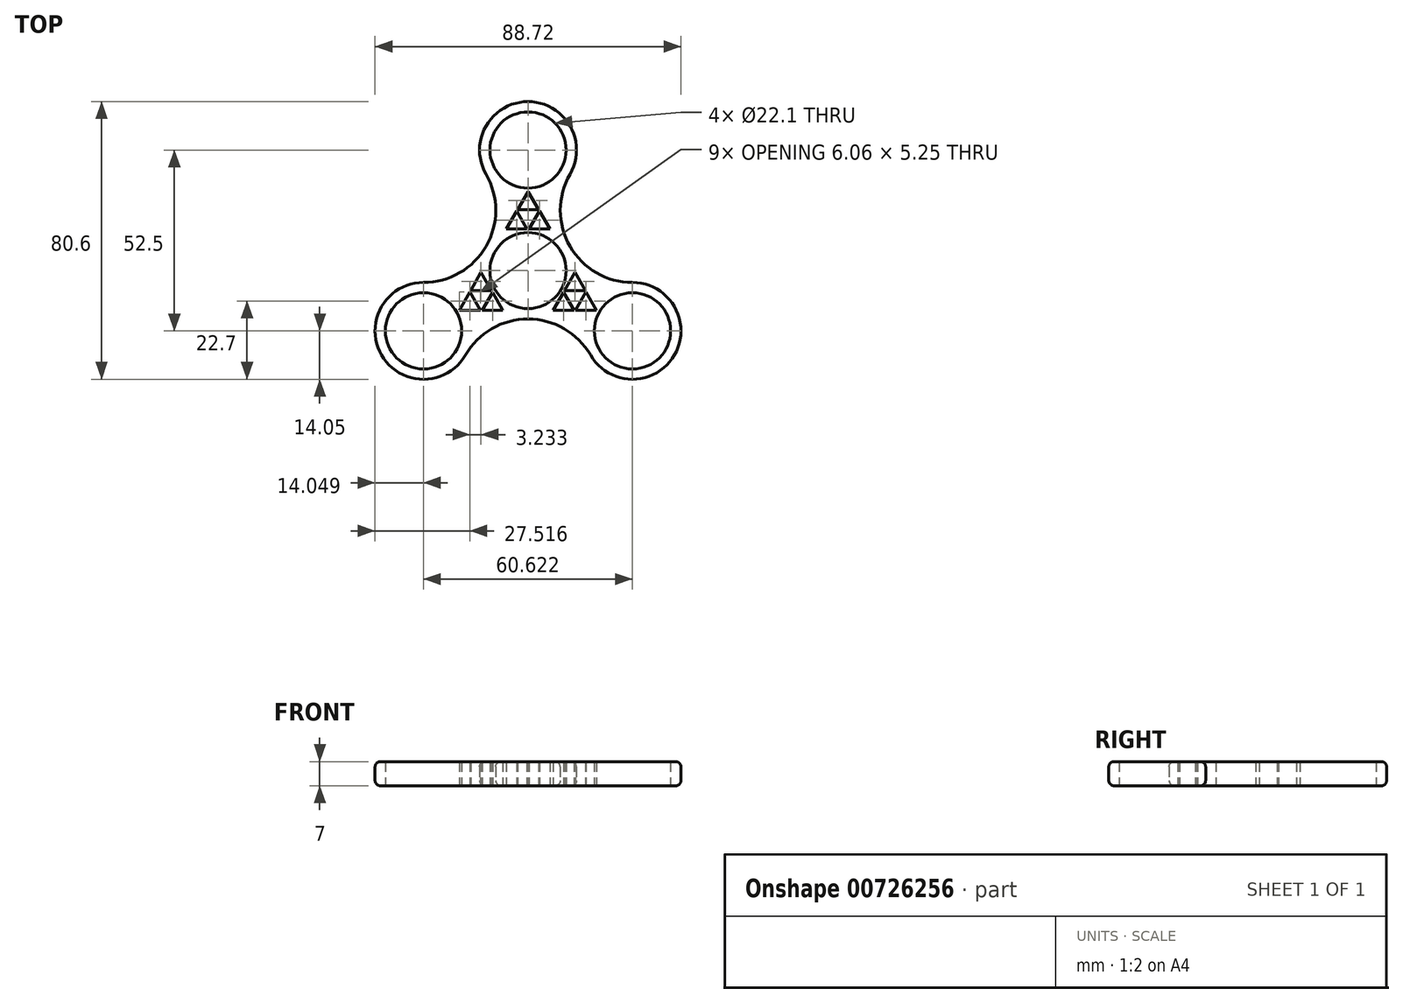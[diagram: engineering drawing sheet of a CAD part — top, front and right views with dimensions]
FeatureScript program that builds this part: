
annotation { "Feature Type Name" : "Feature", "Feature Type Description" : "" }
export const myFeature = defineFeature(function(context is Context, id is Id, definition is map)
    precondition{}
    {
        {
            var Q0;
            Q0=qCreatedBy(makeId("Top.planeOp"),FACE);
            var sketch = newSketch(context, id + "F0", { "sketchPlane" : qUnion([Q0])});
            skCircle(sketch, "E0", {"center": v(0, 0) * mm, "radius": 11.05 * mm});
            skCircle(sketch, "E1", {"center": v(0, 35) * mm, "radius": 11.05 * mm});
            skCircle(sketch, "E2.1.0", {"center": v(-30.31, -17.5) * mm, "radius": 11.05 * mm});
            skCircle(sketch, "E2.2.0", {"center": v(30.31, -17.5) * mm, "radius": 11.05 * mm});
            skArc(sketch, "E3", {"start": v(-30.31, -3.45) * mm, "mid": v(-42.48, -24.52) * mm, "end": v(-18.14, -24.53) * mm});
            skArc(sketch, "E4", {"start": v(12.17, 27.98) * mm, "mid": v(0, 49.05) * mm, "end": v(-12.17, 27.98) * mm});
            skArc(sketch, "E5", {"start": v(18.14, -24.53) * mm, "mid": v(42.48, -24.53) * mm, "end": v(30.31, -3.45) * mm});
            skArc(sketch, "E6", {"start": v(-30.31, -3.45) * mm, "mid": v(-12.17, 7.02) * mm, "end": v(-12.17, 27.98) * mm});
            skArc(sketch, "E7", {"start": v(12.17, 27.98) * mm, "mid": v(12.17, 7.02) * mm, "end": v(30.31, -3.45) * mm});
            skArc(sketch, "E8", {"start": v(18.14, -24.53) * mm, "mid": v(0, -14.05) * mm, "end": v(-18.14, -24.52) * mm});
            skLineSegment(sketch, "E9", {"start": v(-30.31, -17.5) * mm, "end": v(0, 0) * mm, "construction": true});
            skLineSegment(sketch, "E10", {"start": v(0, 35) * mm, "end": v(0, 0) * mm, "construction": true});
            skLineSegment(sketch, "E11", {"start": v(30.31, -17.5) * mm, "end": v(0, 0) * mm, "construction": true});
            skArc(sketch, "E12.cCircle", {"start": v(3.16, 17.3) * mm, "mid": v(3.13, 17.36) * mm, "end": v(3.1, 17.42) * mm, "construction": true});
            skLineSegment(sketch, "E12.2", {"start": v(3.1, 17.42) * mm, "end": v(3.02, 17.29) * mm});
            skCircle(sketch, "E13.cCircle", {"center": v(0, 19.45) * mm, "radius": 3.5 * mm, "construction": true});
            skLineSegment(sketch, "E13.0", {"start": v(0, 22.95) * mm, "end": v(3.03, 17.7) * mm});
            skLineSegment(sketch, "E13.1", {"start": v(3.03, 17.7) * mm, "end": v(-3.03, 17.7) * mm});
            skLineSegment(sketch, "E13.2", {"start": v(-3.03, 17.7) * mm, "end": v(0, 22.95) * mm});
            skCircle(sketch, "E14.cCircle", {"center": v(-3.32, 13.8) * mm, "radius": 3.5 * mm, "construction": true});
            skLineSegment(sketch, "E14.0", {"start": v(-6.35, 12.05) * mm, "end": v(-3.32, 17.3) * mm});
            skLineSegment(sketch, "E14.1", {"start": v(-3.32, 17.3) * mm, "end": v(-0.29, 12.05) * mm});
            skLineSegment(sketch, "E14.2", {"start": v(-0.29, 12.05) * mm, "end": v(-6.35, 12.05) * mm});
            skArc(sketch, "E15.cCircle", {"start": v(2.72, 17.25) * mm, "mid": v(3.77, 10.33) * mm, "end": v(3.02, 17.29) * mm, "construction": true});
            skLineSegment(sketch, "E15.0", {"start": v(6.35, 12.05) * mm, "end": v(0.29, 12.05) * mm});
            skLineSegment(sketch, "E15.1", {"start": v(0.29, 12.05) * mm, "end": v(3.32, 17.3) * mm});
            skLineSegment(sketch, "E15.2", {"start": v(3.32, 17.3) * mm, "end": v(6.35, 12.05) * mm});
            skArc(sketch, "E16.trimOffspring", {"start": v(-3.03, 17.55) * mm, "mid": v(-3.13, 17.43) * mm, "end": v(-3.23, 17.3) * mm, "construction": true});
            skArc(sketch, "E17.trimOffspring", {"start": v(-0.14, 11.8) * mm, "mid": v(0, 11.8) * mm, "end": v(0.16, 11.82) * mm, "construction": true});
            skLineSegment(sketch, "E18.trimOffspring", {"start": v(-3.02, 17.29) * mm, "end": v(-3.03, 17.55) * mm});
            skPoint(sketch, "E19.trimOffspring.end.orphan", {"position": v(0, 12.3) * mm});
            skLineSegment(sketch, "E20.1.0", {"start": v(-13.81, -11.47) * mm, "end": v(-19.88, -11.47) * mm});
            skLineSegment(sketch, "E20.1.1", {"start": v(-19.88, -11.47) * mm, "end": v(-16.84, -6.22) * mm});
            skLineSegment(sketch, "E20.1.2", {"start": v(-16.84, -6.22) * mm, "end": v(-13.81, -11.47) * mm});
            skLineSegment(sketch, "E20.1.3", {"start": v(-13.32, -11.53) * mm, "end": v(-10.3, -6.27) * mm});
            skLineSegment(sketch, "E20.1.4", {"start": v(-7.26, -11.52) * mm, "end": v(-13.32, -11.53) * mm});
            skLineSegment(sketch, "E20.1.5", {"start": v(-10.3, -6.27) * mm, "end": v(-7.26, -11.52) * mm});
            skLineSegment(sketch, "E20.1.6", {"start": v(-10.58, -5.77) * mm, "end": v(-16.64, -5.77) * mm});
            skLineSegment(sketch, "E20.1.7", {"start": v(-16.64, -5.77) * mm, "end": v(-13.61, -0.52) * mm});
            skLineSegment(sketch, "E20.1.8", {"start": v(-13.61, -0.52) * mm, "end": v(-10.58, -5.77) * mm});
            skLineSegment(sketch, "E20.2.0", {"start": v(16.84, -6.23) * mm, "end": v(19.88, -11.48) * mm});
            skLineSegment(sketch, "E20.2.1", {"start": v(19.88, -11.48) * mm, "end": v(13.81, -11.48) * mm});
            skLineSegment(sketch, "E20.2.2", {"start": v(13.81, -11.48) * mm, "end": v(16.84, -6.23) * mm});
            skLineSegment(sketch, "E20.2.3", {"start": v(16.64, -5.77) * mm, "end": v(10.58, -5.78) * mm});
            skLineSegment(sketch, "E20.2.4", {"start": v(13.61, -0.52) * mm, "end": v(16.64, -5.77) * mm});
            skLineSegment(sketch, "E20.2.5", {"start": v(10.58, -5.77) * mm, "end": v(13.61, -0.52) * mm});
            skLineSegment(sketch, "E20.2.6", {"start": v(10.3, -6.28) * mm, "end": v(13.32, -11.53) * mm});
            skLineSegment(sketch, "E20.2.7", {"start": v(13.32, -11.53) * mm, "end": v(7.26, -11.53) * mm});
            skLineSegment(sketch, "E20.2.8", {"start": v(7.26, -11.53) * mm, "end": v(10.3, -6.28) * mm});
            skSolve(sketch);
        }
        {
            var Q0;
            Q0=qSketchRegion(id+"F0",true);
            extrude(context, id + "F1", {"entities" : qUnion([Q0]), "depth" : 7 * mm, "offsetDistance" : 25 * mm});
        }
        {
            var Q0;
            Q0=makeQuery(id+"F1.opExtrude","CAP_EDGE",EDGE,{"disambiguationData":[OSD([sQuery(id+"F0.wireOp",EDGE,"E8")])],"isStart":false});
            var Q1;
            Q1=makeQuery(id+"F1.opExtrude","CAP_EDGE",EDGE,{"disambiguationData":[OSD([sQuery(id+"F0.wireOp",EDGE,"E8")])],"isStart":true});
            fillet(context, id + "F2", {"entities" : qUnion([Q0, Q1]), "radius" : 1.5 * mm, "tangentPropagation" : true, "allowEdgeOverflow" : false});
        }
    });
